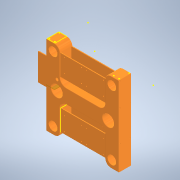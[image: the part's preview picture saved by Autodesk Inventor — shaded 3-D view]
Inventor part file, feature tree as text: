
AUTODESK INVENTOR PART (.ipt)
format: ipt  version: 2021 (Build 250183000, 183)  size: 391,168 bytes
history: native  units: mm
features: sketch x18, extrude x13, reference x7, other x5, projected_geometry x3, plane x2, mirror x2
ambient origin geometry x8: Origin, YZ Plane, XZ Plane, XY Plane, X Axis, Y Axis, Z Axis, Center Point
bodies: Solid1 (feature_tree)
feature tree (50):
  other  "servoMountBar"
  plane  "Work Plane1"
  extrude  "Extrusion7"  Depth=10.0mm TaperAngle=0.0deg
  sketch  "Sketch9"  dims[d19=-141.25mm d21=3.0mm]
  sketch  "Sketch10"  dims[d22=73.5mm d23=3.0mm]
  extrude  "Extrusion8"  Depth=3.0mm
  plane  "Work Plane2"
  mirror  "Mirror1"
  sketch  "Sketch12"  dims[d26=95.5mm d27=70.0mm d28=0.0mm]
  extrude  "Extrusion9"  Depth=3.0mm
  extrude  "Extrusion10"  Depth=3.0mm
  extrude  "Extrusion11"  Depth=70.0mm TaperAngle=0.0deg
  extrude  "Extrusion12"  Depth=50.0mm TaperAngle=0.0deg
  extrude  "Extrusion13"  Depth=43.0mm TaperAngle=0.0deg
  mirror  "Mirror2"
  extrude  "Extrusion14"  Depth=5.0mm
  extrude  "Extrusion15"  Depth=3.0mm
  sketch  "Sketch20"  dims[d51=15.0mm d52=0.0mm d53=25.0mm]
  extrude  "Extrusion16"  Depth=5.0mm
  extrude  "Extrusion17"  Depth=16.0mm TaperAngle=0.0deg
  extrude  "Extrusion18"  Depth=40.0mm
  sketch  "Sketch24"  dims[d57=50.0mm d58=0.0mm]
  extrude  "Extrusion19"  Depth=25.0mm
  sketch  "Sketch8"  dims[d14=15.0mm d15=0.0mm d17=10.0mm d18=0.0mm]
  reference  "Reference32"
  reference  "Reference33"
  reference  "Reference34"
  reference  "Reference35"
  projected_geometry  "Projected Loop5"
  reference  "Reference36"
  reference  "Reference37"
  reference  "Reference38"
  projected_geometry  "Projected Loop6"
  sketch  "Sketch11"  dims[d24=73.5mm d25=3.0mm]
  sketch  "Sketch13"  dims[d29=0.0mm d30=0.0mm d31=50.0mm d32=0.0mm]
  sketch  "Sketch14"  dims[d33=10.0mm d34=43.0mm d35=0.0mm]
  sketch  "Sketch15"  dims[d36=43.0mm d37=0.0mm d38=5.0mm]
  sketch  "Sketch16"  dims[d39=40.0mm d40=0.0mm d41=3.0mm]
  sketch  "Sketch17"  dims[d42=40.0mm d43=0.0mm d44=5.0mm]
  sketch  "Sketch18"  dims[d45=5.0mm d46=16.0mm d47=0.0mm]
  projected_geometry  "Projected Loop7"
  sketch  "Sketch19"  dims[d48=15.0mm d49=40.0mm d50=-1.0mm]
  sketch  "Sketch21"  dims[d54=25.0mm]
  sketch  "Sketch22"  dims[d55=22.0mm]
  sketch  "Sketch23"  dims[d56=22.0mm]
  sketch  "Sketch25"
  other  "4_WheelsSwerve01.iam"
  other  "upper-lower form connector:1"
  other  "side upper and lower connector:1"
  other  "side upper and lower connector:4"
